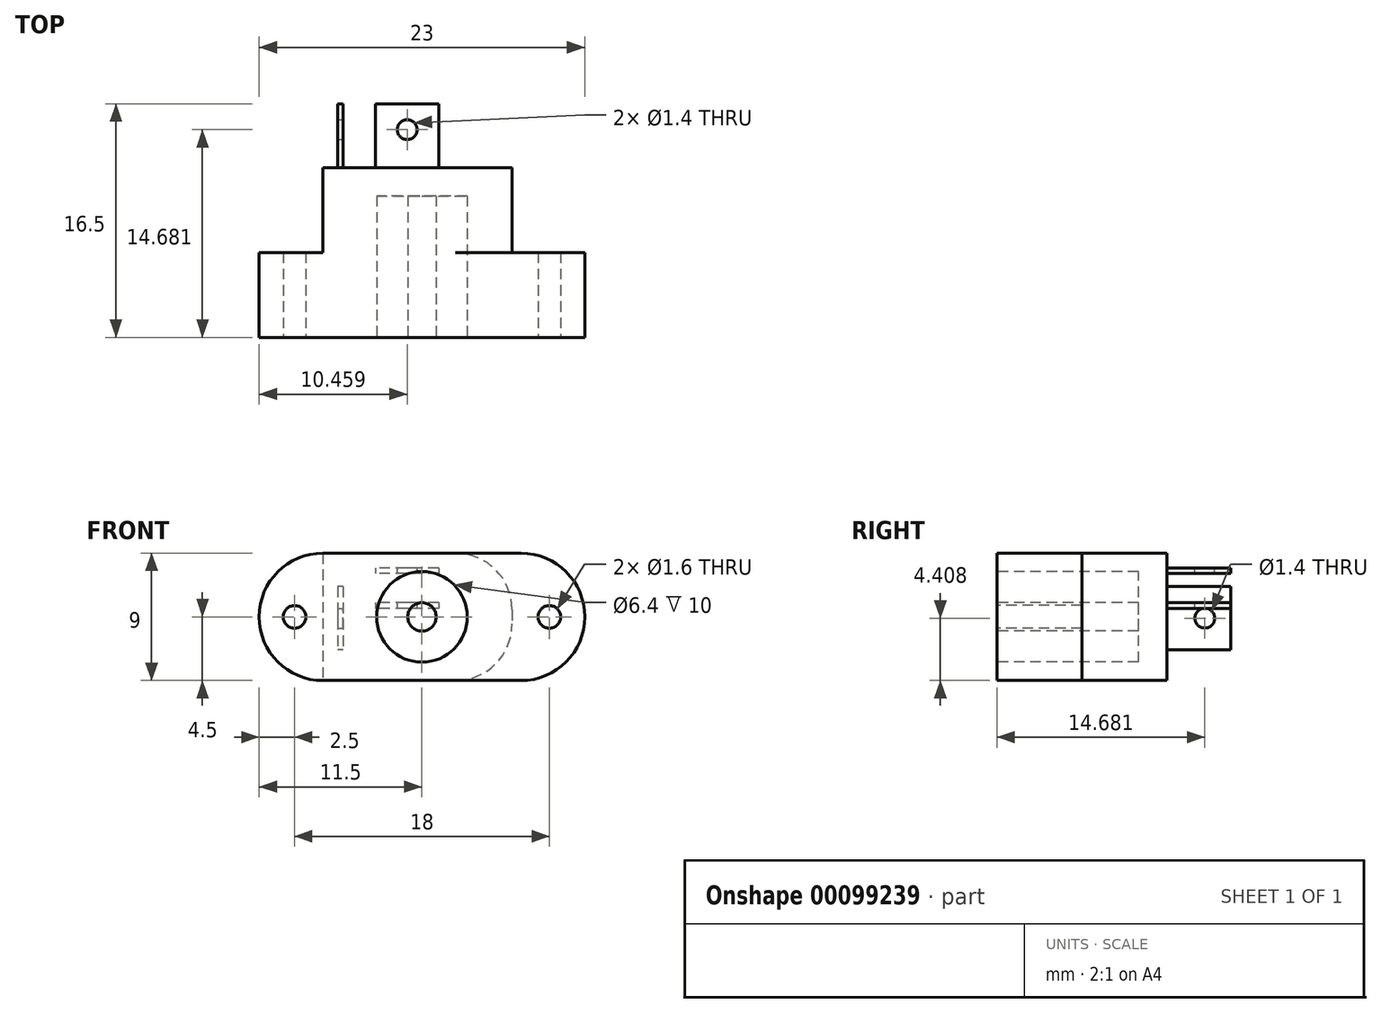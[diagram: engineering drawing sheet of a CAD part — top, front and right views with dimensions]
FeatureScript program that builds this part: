
annotation { "Feature Type Name" : "Feature", "Feature Type Description" : "" }
export const myFeature = defineFeature(function(context is Context, id is Id, definition is map)
    precondition{}
    {
        {
            var Q0;
            Q0=qCreatedBy(makeId("Front.planeOp"),FACE);
            var sketch = newSketch(context, id + "F0", { "sketchPlane" : qUnion([Q0])});
            skLineSegment(sketch, "E0.bottom", {"start": v(7, -4.5) * mm, "end": v(-7, -4.5) * mm});
            skLineSegment(sketch, "E0.top", {"start": v(7, 4.5) * mm, "end": v(-7, 4.5) * mm});
            skLineSegment(sketch, "E0.left", {"start": v(11.5, 0) * mm, "end": v(11.5, 0) * mm});
            skLineSegment(sketch, "E0.right", {"start": v(-11.5, 0) * mm, "end": v(-11.5, 0) * mm});
            skPoint(sketch, "E0.middle", {"position": v(0, 0) * mm});
            skCircle(sketch, "E1", {"center": v(-9, 0) * mm, "radius": 0.8 * mm});
            skCircle(sketch, "E2.MirrorC", {"center": v(9, 0) * mm, "radius": 0.8 * mm});
            skCircle(sketch, "E3", {"center": v(0, 0) * mm, "radius": 3.2 * mm});
            skPoint(sketch, "E4.visualSharp", {"position": v(-11.5, 4.5) * mm});
            skArc(sketch, "E4.filletArc", {"start": v(-7, 4.5) * mm, "mid": v(-10.18, 3.18) * mm, "end": v(-11.5, 0) * mm});
            skPoint(sketch, "E5.visualSharp", {"position": v(-11.5, -4.5) * mm});
            skArc(sketch, "E5.filletArc", {"start": v(-11.5, 0) * mm, "mid": v(-10.18, -3.18) * mm, "end": v(-7, -4.5) * mm});
            skPoint(sketch, "E6.visualSharp", {"position": v(11.5, 4.5) * mm});
            skArc(sketch, "E6.filletArc", {"start": v(11.5, 0) * mm, "mid": v(10.18, 3.18) * mm, "end": v(7, 4.5) * mm});
            skPoint(sketch, "E7.visualSharp", {"position": v(11.5, -4.5) * mm});
            skArc(sketch, "E7.filletArc", {"start": v(7, -4.5) * mm, "mid": v(10.18, -3.18) * mm, "end": v(11.5, 0) * mm});
            skCircle(sketch, "E8", {"center": v(0, 0) * mm, "radius": 1 * mm});
            skSolve(sketch);
        }
        {
            var Q0;
            Q0=makeQuery(id+"F0.imprint","IMPRINT",FACE,{"disambiguationData":[TD([[makeQuery(id+"F0.imprint","IMPRINT",EDGE,{"derivedFrom":sQuery(id+"F0.wireOp",EDGE,"E0.bottom")}),-1.0]])]});
            extrude(context, id + "F1", {"entities" : qUnion([Q0]), "oppositeDirection" : true, "depth" : 6 * mm});
        }
        {
            var Q0;
            Q0=makeQuery(id+"F1.opExtrude","CAP_FACE",FACE,{"disambiguationData":[OSD([sQuery(id+"F0.wireOp",EDGE,"E0.bottom"),sQuery(id+"F0.wireOp",EDGE,"E0.top"),sQuery(id+"F0.wireOp",EDGE,"E1"),sQuery(id+"F0.wireOp",EDGE,"E2.MirrorC"),sQuery(id+"F0.wireOp",EDGE,"E3"),sQuery(id+"F0.wireOp",EDGE,"E4.filletArc"),sQuery(id+"F0.wireOp",EDGE,"E5.filletArc"),sQuery(id+"F0.wireOp",EDGE,"E6.filletArc"),sQuery(id+"F0.wireOp",EDGE,"E7.filletArc")])],"isStart":false});
            var sketch = newSketch(context, id + "F2", { "sketchPlane" : qUnion([Q0])});
            skLineSegment(sketch, "E9.bottom", {"start": v(-2.37, 4.5) * mm, "end": v(7, 4.5) * mm});
            skLineSegment(sketch, "E9.top", {"start": v(-2.37, -4.5) * mm, "end": v(7, -4.5) * mm});
            skLineSegment(sketch, "E9.left", {"start": v(-6.37, 0.5) * mm, "end": v(-6.37, -0.5) * mm});
            skLineSegment(sketch, "E9.right", {"start": v(7, 4.5) * mm, "end": v(7, -4.5) * mm});
            skPoint(sketch, "E10.visualSharp", {"position": v(-6.37, 4.5) * mm});
            skArc(sketch, "E10.filletArc", {"start": v(-2.37, 4.5) * mm, "mid": v(-5.2, 3.33) * mm, "end": v(-6.37, 0.5) * mm});
            skPoint(sketch, "E11.visualSharp", {"position": v(-6.37, -4.5) * mm});
            skArc(sketch, "E11.filletArc", {"start": v(-6.37, -0.5) * mm, "mid": v(-5.2, -3.33) * mm, "end": v(-2.37, -4.5) * mm});
            skSolve(sketch);
        }
        {
            var Q0;
            Q0 = qSketchRegion(id + "F2", true);
            extrude(context, id + "F3", {"entities" : qUnion([Q0]), "operationType" : NewBodyOperationType.ADD, "depth" : 6 * mm});
        }
        {
            var Q0;
            Q0=makeQuery(id+"F3.opExtrude","CAP_FACE",FACE,{"disambiguationData":[OSD([sQuery(id+"F2.wireOp",EDGE,"E9.bottom"),sQuery(id+"F2.wireOp",EDGE,"E9.top"),sQuery(id+"F2.wireOp",EDGE,"E9.left"),sQuery(id+"F2.wireOp",EDGE,"E9.right"),sQuery(id+"F2.wireOp",EDGE,"E10.filletArc"),sQuery(id+"F2.wireOp",EDGE,"E11.filletArc")])],"isStart":false});
            var sketch = newSketch(context, id + "F4", { "sketchPlane" : qUnion([Q0])});
            skLineSegment(sketch, "E12.bottom", {"start": v(-1.2, 3.46) * mm, "end": v(3.27, 3.46) * mm});
            skLineSegment(sketch, "E12.top", {"start": v(-1.2, 3.06) * mm, "end": v(3.27, 3.06) * mm});
            skLineSegment(sketch, "E12.left", {"start": v(-1.2, 3.46) * mm, "end": v(-1.2, 3.06) * mm});
            skLineSegment(sketch, "E12.right", {"start": v(3.27, 3.46) * mm, "end": v(3.27, 3.06) * mm});
            skLineSegment(sketch, "E13.bottom", {"start": v(-1.2, 1) * mm, "end": v(3.27, 1) * mm});
            skLineSegment(sketch, "E13.top", {"start": v(-1.2, 0.6) * mm, "end": v(3.27, 0.6) * mm});
            skLineSegment(sketch, "E13.left", {"start": v(-1.2, 1) * mm, "end": v(-1.2, 0.6) * mm});
            skLineSegment(sketch, "E13.right", {"start": v(3.27, 1) * mm, "end": v(3.27, 0.6) * mm});
            skLineSegment(sketch, "E14.bottom", {"start": v(5.56, 2.14) * mm, "end": v(5.96, 2.14) * mm});
            skLineSegment(sketch, "E14.top", {"start": v(5.56, -2.32) * mm, "end": v(5.96, -2.32) * mm});
            skLineSegment(sketch, "E14.left", {"start": v(5.56, 2.14) * mm, "end": v(5.56, -2.32) * mm});
            skLineSegment(sketch, "E14.right", {"start": v(5.96, 2.14) * mm, "end": v(5.96, -2.32) * mm});
            skSolve(sketch);
        }
        {
            var Q0;
            Q0 = qSketchRegion(id + "F4", true);
            var Q1;
            Q1 = qConstructionFilter(qBodyType(qCreatedBy(id + "F4" ,EDGE), BodyType.WIRE), ConstructionObject.NO);
            extrude(context, id + "F5", {"entities" : qUnion([Q0]), "operationType" : NewBodyOperationType.ADD, "surfaceEntities" : qUnion([Q1]), "depth" : 4.5 * mm});
        }
        {
            var Q0;
            Q0=makeQuery(id+"F5.opExtrude","SWEPT_FACE",FACE,{"disambiguationData":[OSD([sQuery(id+"F4.wireOp",EDGE,"E12.bottom")])]});
            var sketch = newSketch(context, id + "F6", { "sketchPlane" : qUnion([Q0])});
            skCircle(sketch, "E15", {"center": v(-1.04, 14.68) * mm, "radius": 0.7 * mm});
            skLineSegment(sketch, "E16", {"start": v(-3.27, 14.68) * mm, "end": v(-1.04, 14.68) * mm, "construction": true});
            skLineSegment(sketch, "E17", {"start": v(-1.04, 14.68) * mm, "end": v(1.2, 14.68) * mm, "construction": true});
            skLineSegment(sketch, "E18", {"start": v(-1.04, 14.68) * mm, "end": v(-1.04, 16.5) * mm, "construction": true});
            skSolve(sketch);
        }
        {
            var Q0;
            Q0 = qSketchRegion(id + "F6", true);
            extrude(context, id + "F7", {"entities" : qUnion([Q0]), "operationType" : NewBodyOperationType.REMOVE, "oppositeDirection" : true, "depth" : 5 * mm});
        }
        {
            var Q0;
            Q0=makeQuery(id+"F5.opExtrude","SWEPT_FACE",FACE,{"disambiguationData":[OSD([sQuery(id+"F4.wireOp",EDGE,"E14.left")])]});
            var sketch = newSketch(context, id + "F8", { "sketchPlane" : qUnion([Q0])});
            skCircle(sketch, "E19", {"center": v(14.68, -0.1) * mm, "radius": 0.7 * mm});
            skLineSegment(sketch, "E20", {"start": v(14.68, 2.14) * mm, "end": v(14.68, -0.1) * mm, "construction": true});
            skLineSegment(sketch, "E21", {"start": v(14.68, -0.1) * mm, "end": v(16.5, -0.1) * mm, "construction": true});
            skLineSegment(sketch, "E22", {"start": v(14.68, -0.1) * mm, "end": v(14.68, -2.32) * mm, "construction": true});
            skSolve(sketch);
        }
        {
            var Q0;
            Q0 = qSketchRegion(id + "F8", true);
            extrude(context, id + "F9", {"entities" : qUnion([Q0]), "operationType" : NewBodyOperationType.REMOVE, "oppositeDirection" : true, "depth" : 1 * mm});
        }
        {
            var Q0;
            Q0=makeQuery(id+"F0.imprint","IMPRINT",FACE,{"disambiguationData":[TD([[makeQuery(id+"F0.imprint","IMPRINT",EDGE,{"derivedFrom":sQuery(id+"F0.wireOp",EDGE,"E3")}),1.0]])]});
            extrude(context, id + "F10", {"entities" : qUnion([Q0]), "operationType" : NewBodyOperationType.REMOVE, "oppositeDirection" : true, "depth" : 10 * mm});
        }
        {
            var Q0;
            Q0=makeQuery(id+"F0.imprint","IMPRINT",FACE,{"disambiguationData":[TD([[makeQuery(id+"F0.imprint","IMPRINT",EDGE,{"derivedFrom":sQuery(id+"F0.wireOp",EDGE,"E8")}),1.0]])]});
            var Q1;
            Q1=sQuery(id+"F0.wireOp",EDGE,"E8");
            extrude(context, id + "F11", {"entities" : qUnion([Q0]), "operationType" : NewBodyOperationType.ADD, "surfaceEntities" : qUnion([Q1]), "oppositeDirection" : true, "depth" : 10 * mm});
        }
    });
